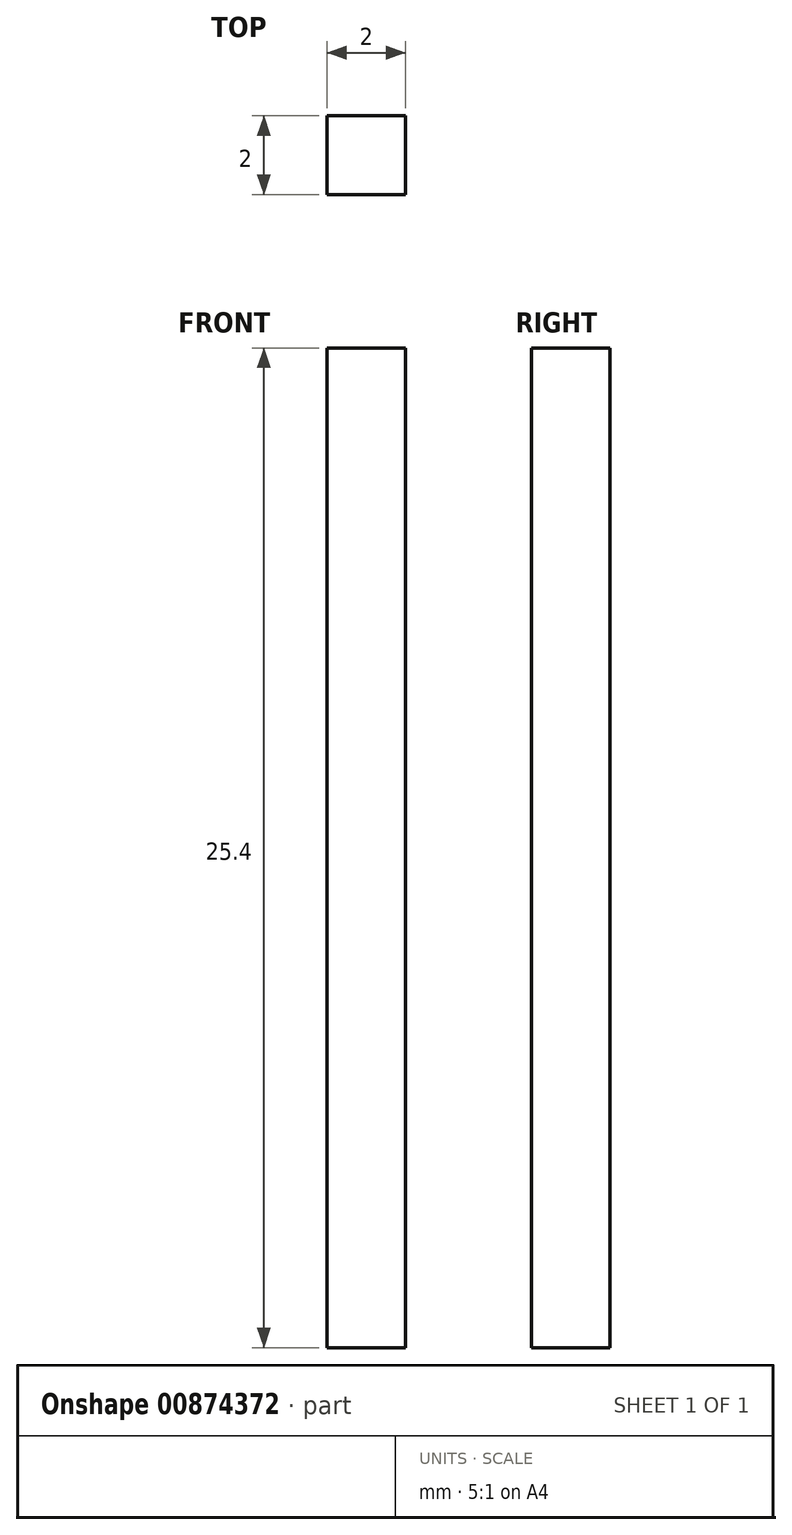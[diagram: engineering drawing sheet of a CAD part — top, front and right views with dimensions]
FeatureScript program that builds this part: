
annotation { "Feature Type Name" : "Feature", "Feature Type Description" : "" }
export const myFeature = defineFeature(function(context is Context, id is Id, definition is map)
    precondition{}
    {
        {
            var Q0;
            Q0=qCreatedBy(makeId("Top.planeOp"),FACE);
            var sketch = newSketch(context, id + "F0", { "sketchPlane" : qUnion([Q0])});
            skLineSegment(sketch, "E0.bottom", {"start": v(1, 1) * mm, "end": v(-1, 1) * mm});
            skLineSegment(sketch, "E0.top", {"start": v(1, -1) * mm, "end": v(-1, -1) * mm});
            skLineSegment(sketch, "E0.left", {"start": v(1, 1) * mm, "end": v(1, -1) * mm});
            skLineSegment(sketch, "E0.right", {"start": v(-1, 1) * mm, "end": v(-1, -1) * mm});
            skPoint(sketch, "E0.middle", {"position": v(0, 0) * mm});
            skSolve(sketch);
        }
        {
            var Q0;
            Q0=makeQuery(id+"F0.imprint","IMPRINT",FACE,{"disambiguationData":[TD([[makeQuery(id+"F0.imprint","IMPRINT",EDGE,{"derivedFrom":sQuery(id+"F0.wireOp",EDGE,"E0.bottom")}),1.0]])]});
            extrude(context, id + "F1", {"entities" : qUnion([Q0]), "depth" : 25.4 * mm, "offsetDistance" : 25.4 * mm});
        }
    });
